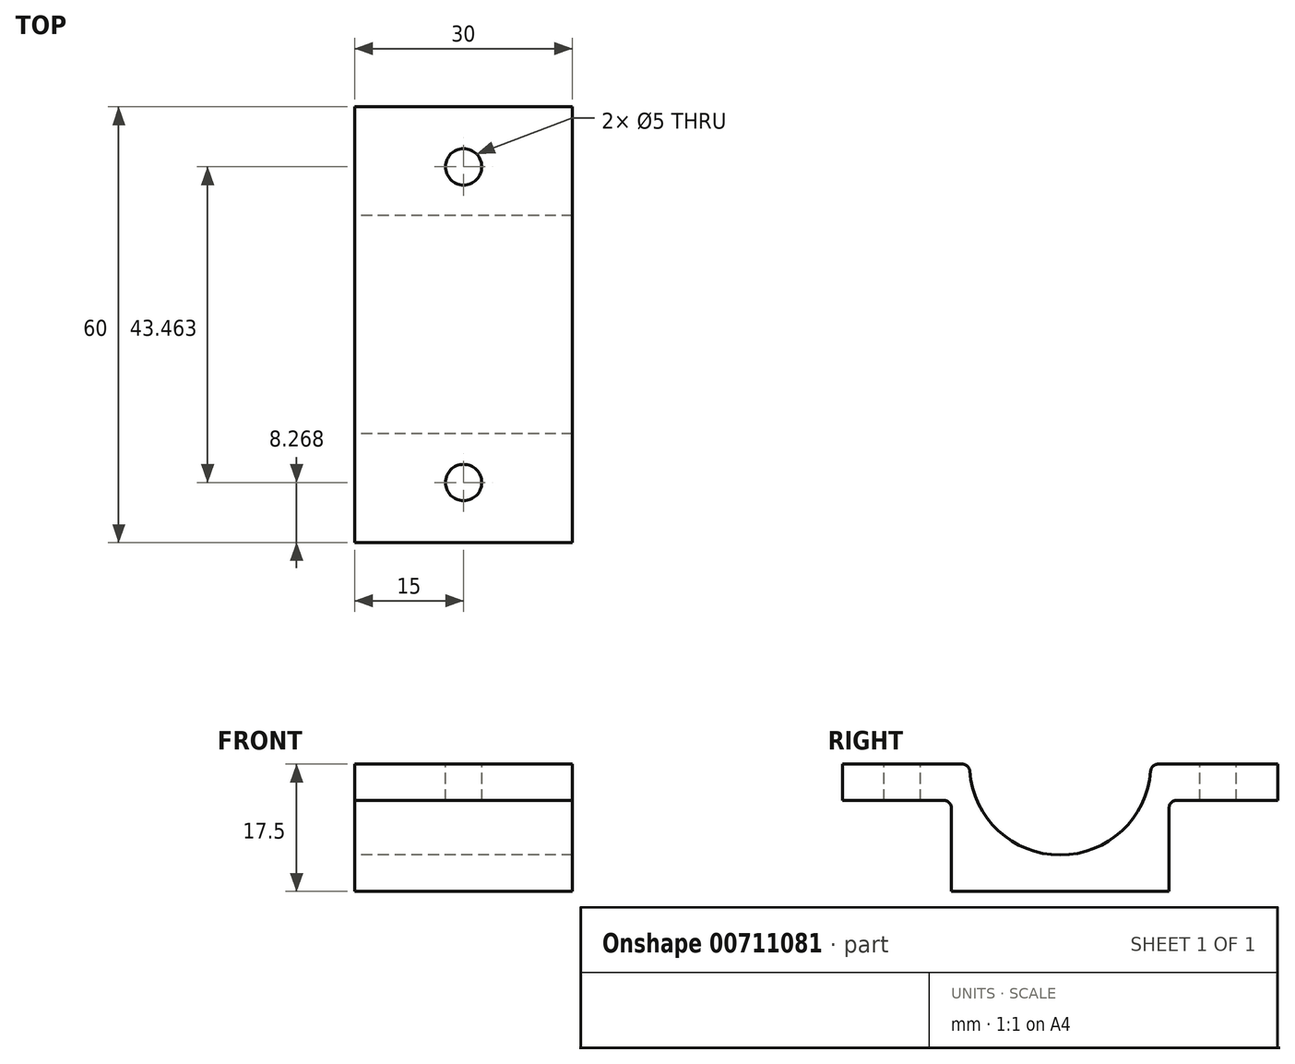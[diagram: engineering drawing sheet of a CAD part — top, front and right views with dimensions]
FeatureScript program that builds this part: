
annotation { "Feature Type Name" : "Feature", "Feature Type Description" : "" }
export const myFeature = defineFeature(function(context is Context, id is Id, definition is map)
    precondition{}
    {
        {
            var Q0;
            Q0=qCreatedBy(makeId("Top.planeOp"),FACE);
            var sketch = newSketch(context, id + "F0", { "sketchPlane" : qUnion([Q0])});
            skLineSegment(sketch, "E0.bottom", {"start": v(15, 15) * mm, "end": v(-15, 15) * mm});
            skLineSegment(sketch, "E0.top", {"start": v(15, -15) * mm, "end": v(-15, -15) * mm});
            skLineSegment(sketch, "E0.left", {"start": v(15, 15) * mm, "end": v(15, -15) * mm});
            skLineSegment(sketch, "E0.right", {"start": v(-15, 15) * mm, "end": v(-15, -15) * mm});
            skPoint(sketch, "E0.middle", {"position": v(0, 0) * mm});
            skSolve(sketch);
        }
        {
            var Q0;
            Q0=makeQuery(id+"F0.imprint","IMPRINT",FACE,{"disambiguationData":[TD([[makeQuery(id+"F0.imprint","IMPRINT",EDGE,{"derivedFrom":sQuery(id+"F0.wireOp",EDGE,"E0.bottom")}),1.0]])]});
            extrude(context, id + "F1", {"entities" : qUnion([Q0]), "oppositeDirection" : true, "depth" : 5 * mm, "offsetDistance" : 25 * mm});
        }
        {
            var Q0;
            Q0=makeQuery(id+"F1.opExtrude","SWEPT_FACE",FACE,{"disambiguationData":[OSD([sQuery(id+"F0.wireOp",EDGE,"E0.right")])]});
            var sketch = newSketch(context, id + "F2", { "sketchPlane" : qUnion([Q0])});
            skArc(sketch, "E1", {"start": v(-12.5, 12.5) * mm, "mid": v(0, 0) * mm, "end": v(12.5, 12.5) * mm});
            skLineSegment(sketch, "E2", {"start": v(-15, 12.5) * mm, "end": v(-15, 12.5) * mm});
            skLineSegment(sketch, "E3", {"start": v(-15, 12.5) * mm, "end": v(-15, 0) * mm});
            skLineSegment(sketch, "E4", {"start": v(15, 12.5) * mm, "end": v(15, 0) * mm});
            skLineSegment(sketch, "E5", {"start": v(-15, 12.5) * mm, "end": v(15, 12.5) * mm});
            skLineSegment(sketch, "E6.trimOffspring", {"start": v(15, 12.5) * mm, "end": v(15, 12.5) * mm});
            skLineSegment(sketch, "E7.bottom", {"start": v(-15, 12.5) * mm, "end": v(-30, 12.5) * mm});
            skLineSegment(sketch, "E7.top", {"start": v(-15, 7.5) * mm, "end": v(-30, 7.5) * mm});
            skLineSegment(sketch, "E7.left", {"start": v(-15, 12.5) * mm, "end": v(-15, 7.5) * mm});
            skLineSegment(sketch, "E7.right", {"start": v(-30, 12.5) * mm, "end": v(-30, 7.5) * mm});
            skLineSegment(sketch, "E8.bottom", {"start": v(15, 12.5) * mm, "end": v(30, 12.5) * mm});
            skLineSegment(sketch, "E8.top", {"start": v(15, 7.5) * mm, "end": v(30, 7.5) * mm});
            skLineSegment(sketch, "E8.left", {"start": v(15, 12.5) * mm, "end": v(15, 7.5) * mm});
            skLineSegment(sketch, "E8.right", {"start": v(30, 12.5) * mm, "end": v(30, 7.5) * mm});
            skSolve(sketch);
        }
        {
            var Q0;
            Q0=makeQuery(id+"F2.imprint","IMPRINT",FACE,{"disambiguationData":[TD([[makeQuery(id+"F2.imprint","IMPRINT",EDGE,{"derivedFrom":sQuery(id+"F2.wireOp",EDGE,"E7.bottom")}),1.0]])]});
            var Q1;
            {var subQ4=sQuery(id+"F2.wireOp",EDGE,"E3");Q1=makeQuery(id+"F2.imprint","IMPRINT",FACE,{"disambiguationData":[TD([[makeQuery(id+"F2.imprint","IMPRINT",EDGE,{"derivedFrom":subQ4}),1.0]])]});}
            var Q2;
            {var subQ1=sQuery(id+"F2.wireOp",EDGE,"E4");Q2=makeQuery(id+"F2.imprint","IMPRINT",FACE,{"disambiguationData":[TD([[makeQuery(id+"F2.imprint","IMPRINT",EDGE,{"derivedFrom":subQ1}),-1.0]])]});}
            var Q3;
            Q3=makeQuery(id+"F2.imprint","IMPRINT",FACE,{"disambiguationData":[TD([[makeQuery(id+"F2.imprint","IMPRINT",EDGE,{"derivedFrom":sQuery(id+"F2.wireOp",EDGE,"E8.bottom")}),-1.0]])]});
            extrude(context, id + "F3", {"entities" : qUnion([Q0, Q1, Q2, Q3]), "operationType" : NewBodyOperationType.ADD, "oppositeDirection" : true, "depth" : 30 * mm, "offsetDistance" : 25 * mm});
        }
        {
            var Q0;
            {var subQ0=sQuery(id+"F2.wireOp",EDGE,"E5");var subQ1=sQuery(id+"F2.wireOp",EDGE,"E1");Q0=makeQuery(id+"F3.opExtrude","SWEPT_EDGE",EDGE,{"disambiguationData":[OSD([subQ1,subQ0]),TDD([makeQuery(id+"F2.imprint","INTERSECT",VERTEX,{"disambiguationData":[OD(0.0)],"derivedFrom":[subQ1,subQ0]})])]});}
            var Q1;
            {var subQ0=sQuery(id+"F2.wireOp",EDGE,"E5");var subQ1=sQuery(id+"F2.wireOp",EDGE,"E1");Q1=makeQuery(id+"F3.opExtrude","SWEPT_EDGE",EDGE,{"disambiguationData":[OSD([subQ1,subQ0]),TDD([makeQuery(id+"F2.imprint","INTERSECT",VERTEX,{"disambiguationData":[OD(1.0)],"derivedFrom":[subQ1,subQ0]})])]});}
            var Q2;
            Q2=makeQuery(id+"F3.opExtrude","SWEPT_EDGE",EDGE,{"disambiguationData":[OSD([sQuery(id+"F2.wireOp",EDGE,"E4"),sQuery(id+"F2.wireOp",EDGE,"E8.top"),sQuery(id+"F2.wireOp",EDGE,"E8.left")])]});
            var Q3;
            Q3=makeQuery(id+"F3.opExtrude","SWEPT_EDGE",EDGE,{"disambiguationData":[OSD([sQuery(id+"F2.wireOp",EDGE,"E3"),sQuery(id+"F2.wireOp",EDGE,"E7.top"),sQuery(id+"F2.wireOp",EDGE,"E7.left")])]});
            fillet(context, id + "F4", {"entities" : qUnion([Q0, Q1, Q2, Q3]), "radius" : 1 * mm, "tangentPropagation" : true, "allowEdgeOverflow" : false});
        }
        {
            var Q0;
            Q0=makeQuery(id+"F3.opExtrude","SWEPT_FACE",FACE,{"disambiguationData":[OSD([sQuery(id+"F2.wireOp",EDGE,"E5"),sQuery(id+"F2.wireOp",EDGE,"E8.bottom")])]});
            var sketch = newSketch(context, id + "F5", { "sketchPlane" : qUnion([Q0])});
            skLineSegment(sketch, "E9.0.0", {"start": v(15, -30) * mm, "end": v(15, -13.46) * mm});
            skLineSegment(sketch, "E9.0.1", {"start": v(15, -13.46) * mm, "end": v(-15, -13.46) * mm});
            skLineSegment(sketch, "E9.0.2", {"start": v(-15, -13.46) * mm, "end": v(-15, -30) * mm});
            skLineSegment(sketch, "E9.0.3", {"start": v(-15, -30) * mm, "end": v(15, -30) * mm});
            skLineSegment(sketch, "E10.0.0", {"start": v(-15, 30) * mm, "end": v(-15, 13.46) * mm});
            skLineSegment(sketch, "E10.0.1", {"start": v(-15, 13.46) * mm, "end": v(15, 13.46) * mm});
            skLineSegment(sketch, "E10.0.2", {"start": v(15, 13.46) * mm, "end": v(15, 30) * mm});
            skLineSegment(sketch, "E10.0.3", {"start": v(15, 30) * mm, "end": v(-15, 30) * mm});
            skPoint(sketch, "E11", {"position": v(0, 21.73) * mm});
            skPoint(sketch, "E11.positionSnap0", {"position": v(0, 30) * mm});
            skPoint(sketch, "E11.positionSnap1", {"position": v(-15, 21.73) * mm});
            skPoint(sketch, "E12", {"position": v(0, -21.73) * mm});
            skPoint(sketch, "E12.positionSnap0", {"position": v(-15, -21.73) * mm});
            skSolve(sketch);
        }
        {
            var Q0;
            Q0=sQuery(id+"F5.wireOp",VERTEX,"E11");
            var Q1;
            Q1=sQuery(id+"F5.wireOp",VERTEX,"E12");
            var Q2;
            Q2=makeQuery(id+"F1.opExtrude","SWEPT_BODY",BODY,{"disambiguationData":[OSD([sQuery(id+"F0.wireOp",EDGE,"E0.bottom"),sQuery(id+"F0.wireOp",EDGE,"E0.top"),sQuery(id+"F0.wireOp",EDGE,"E0.left"),sQuery(id+"F0.wireOp",EDGE,"E0.right")])]});
            hole(context, id + "F6", {"style" : HoleStyle.SIMPLE, "endStyle" : HoleEndStyle.THROUGH, "holeDiameter" : 5 * mm, "majorDiameter" : 5 * mm, "isTappedThrough" : true, "tappedDepth" : 12 * mm, "tapClearance" : 3, "locations" : qUnion([Q0, Q1]), "scope" : qUnion([Q2])});
        }
    });
